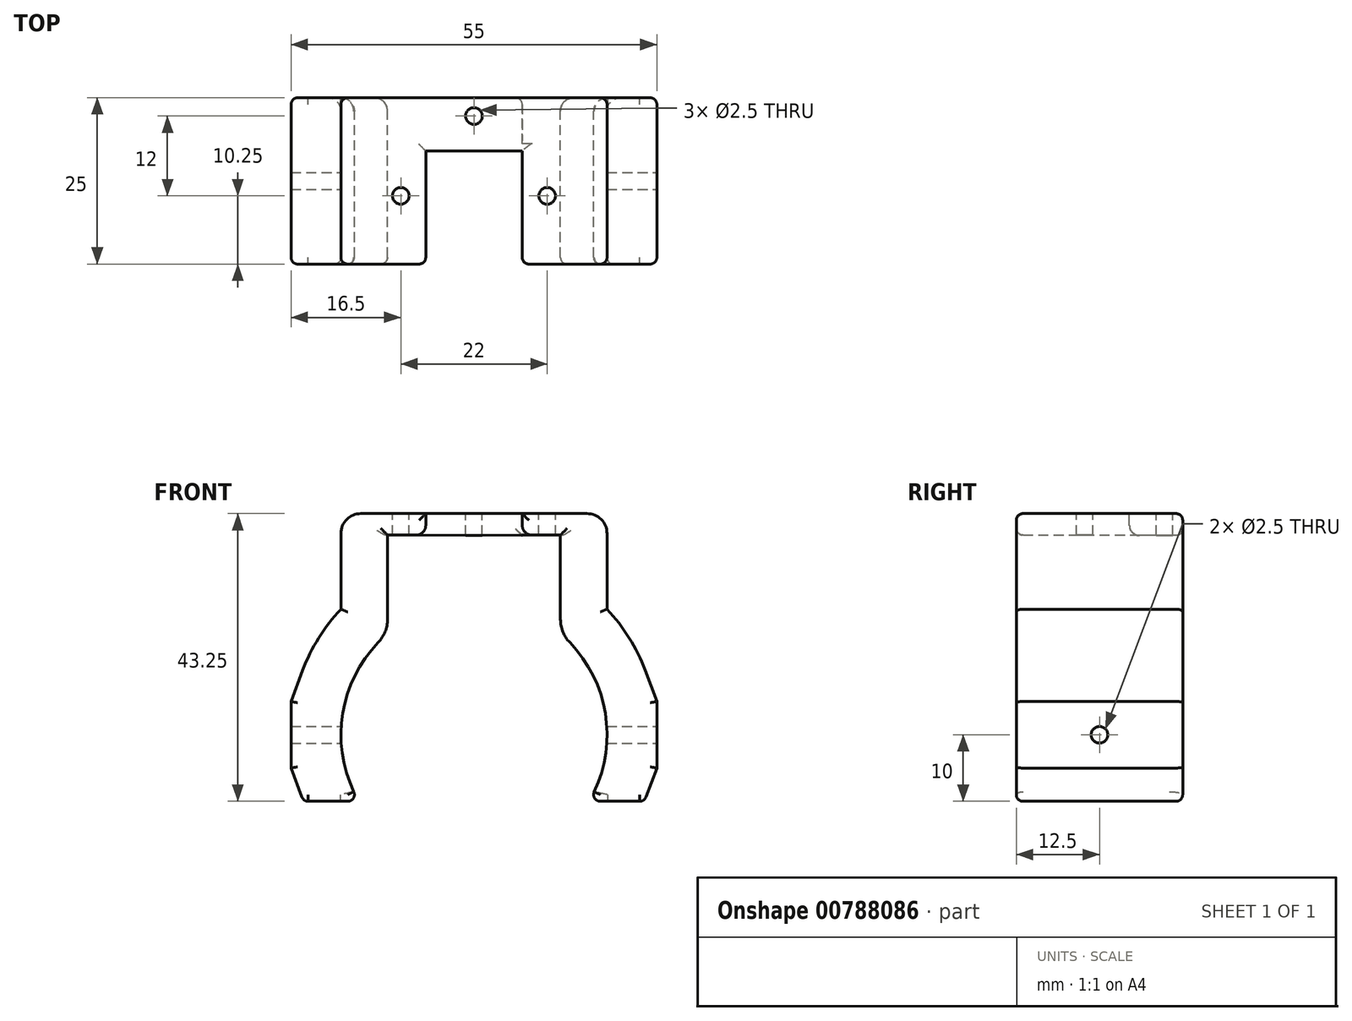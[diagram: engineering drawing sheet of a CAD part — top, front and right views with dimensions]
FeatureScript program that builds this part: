
annotation { "Feature Type Name" : "Feature", "Feature Type Description" : "" }
export const myFeature = defineFeature(function(context is Context, id is Id, definition is map)
    precondition{}
    {
        {
            var Q0;
            Q0=qCreatedBy(makeId("Front.planeOp"),FACE);
            var sketch = newSketch(context, id + "F0", { "sketchPlane" : qUnion([Q0])});
            skLineSegment(sketch, "E0", {"start": v(0, 0) * mm, "end": v(0, 1) * mm});
            skArc(sketch, "E1", {"start": v(-13, 16.2) * mm, "mid": v(0, -19) * mm, "end": v(13, 16.2) * mm});
            skArc(sketch, "E2.0", {"start": v(-20, 19.87) * mm, "mid": v(-23.33, 15.56) * mm, "end": v(-25.74, 10.68) * mm});
            skLineSegment(sketch, "E3", {"start": v(0, 0) * mm, "end": v(0, 15) * mm, "construction": true});
            skLineSegment(sketch, "E4", {"start": v(0, 15) * mm, "end": v(13, 15) * mm, "construction": true});
            skLineSegment(sketch, "E5.MirrorCS", {"start": v(0, 15) * mm, "end": v(-13, 15) * mm, "construction": true});
            skLineSegment(sketch, "E6", {"start": v(27.5, 1) * mm, "end": v(27.5, 6) * mm});
            skLineSegment(sketch, "E7", {"start": v(0, 1) * mm, "end": v(32.41, 1) * mm, "construction": true});
            skLineSegment(sketch, "E8", {"start": v(27.5, 6) * mm, "end": v(25.74, 10.68) * mm});
            skLineSegment(sketch, "E9.MirrorCS", {"start": v(27.5, -4) * mm, "end": v(25.74, -8.68) * mm});
            skLineSegment(sketch, "E10.MirrorCS", {"start": v(27.5, 1) * mm, "end": v(27.5, -4) * mm});
            skArc(sketch, "E11.trimOffspring", {"start": v(25.74, 10.68) * mm, "mid": v(23.33, 15.56) * mm, "end": v(20, 19.87) * mm});
            skLineSegment(sketch, "E12.MirrorCS", {"start": v(-27.5, 6) * mm, "end": v(-25.74, 10.68) * mm});
            skLineSegment(sketch, "E13.MirrorCS", {"start": v(-27.5, 1) * mm, "end": v(-27.5, 6) * mm});
            skLineSegment(sketch, "E14.MirrorCS", {"start": v(-27.5, 1) * mm, "end": v(-27.5, -4) * mm});
            skLineSegment(sketch, "E15.MirrorCS", {"start": v(-27.5, -4) * mm, "end": v(-25.74, -8.68) * mm});
            skArc(sketch, "E16.trimOffspring", {"start": v(-25.74, -8.68) * mm, "mid": v(-19.45, -18.45) * mm, "end": v(-9.68, -24.74) * mm});
            skLineSegment(sketch, "E17", {"start": v(0, 1) * mm, "end": v(-10.04, -9.04) * mm, "construction": true});
            skLineSegment(sketch, "E18.MirrorCS", {"start": v(5, -26.5) * mm, "end": v(9.68, -24.74) * mm});
            skLineSegment(sketch, "E19.MirrorCS", {"start": v(0, -26.5) * mm, "end": v(5, -26.5) * mm});
            skLineSegment(sketch, "E20.MirrorCS", {"start": v(0, -26.5) * mm, "end": v(-5, -26.5) * mm});
            skLineSegment(sketch, "E21.MirrorCS", {"start": v(-5, -26.5) * mm, "end": v(-9.68, -24.74) * mm});
            skArc(sketch, "E22.trimOffspring", {"start": v(9.68, -24.74) * mm, "mid": v(19.45, -18.45) * mm, "end": v(25.74, -8.68) * mm});
            skLineSegment(sketch, "E23", {"start": v(13, 16.2) * mm, "end": v(13, 25.23) * mm});
            skLineSegment(sketch, "E24", {"start": v(-13, 16.2) * mm, "end": v(-13, 25.23) * mm});
            skLineSegment(sketch, "E25", {"start": v(0, 1) * mm, "end": v(0, 31) * mm, "construction": true});
            skLineSegment(sketch, "E26", {"start": v(0, 31) * mm, "end": v(-7.25, 31) * mm, "construction": true});
            skLineSegment(sketch, "E27.MirrorCS", {"start": v(0, 31) * mm, "end": v(7.25, 31) * mm, "construction": true});
            skLineSegment(sketch, "E28", {"start": v(-13, 25.23) * mm, "end": v(-13, 31.02) * mm});
            skLineSegment(sketch, "E29", {"start": v(-13, 31.02) * mm, "end": v(-7.25, 31) * mm});
            skLineSegment(sketch, "E30", {"start": v(-20, 31.05) * mm, "end": v(-20, 19.87) * mm});
            skLineSegment(sketch, "E31", {"start": v(-7.25, 31) * mm, "end": v(-7.25, 34.25) * mm});
            skLineSegment(sketch, "E32", {"start": v(-7.25, 34.25) * mm, "end": v(-20, 34.25) * mm});
            skLineSegment(sketch, "E33", {"start": v(-20, 34.25) * mm, "end": v(-20, 31.05) * mm});
            skLineSegment(sketch, "E34.MirrorCS", {"start": v(13, 25.23) * mm, "end": v(13, 31.02) * mm});
            skLineSegment(sketch, "E35.MirrorCS", {"start": v(13, 31.02) * mm, "end": v(7.25, 31) * mm});
            skLineSegment(sketch, "E36.MirrorCS", {"start": v(7.25, 31) * mm, "end": v(7.25, 34.25) * mm});
            skLineSegment(sketch, "E37.MirrorCS", {"start": v(7.25, 34.25) * mm, "end": v(20, 34.25) * mm});
            skLineSegment(sketch, "E38.MirrorCS", {"start": v(20, 34.25) * mm, "end": v(20, 31.05) * mm});
            skLineSegment(sketch, "E39.MirrorCS", {"start": v(20, 31.05) * mm, "end": v(20, 19.87) * mm});
            skSolve(sketch);
        }
        {
            var Q0;
            Q0=makeQuery(id+"F0.imprint","IMPRINT",FACE,{"disambiguationData":[TD([[makeQuery(id+"F0.imprint","IMPRINT",EDGE,{"derivedFrom":sQuery(id+"F0.wireOp",EDGE,"E1")}),-1.0]])]});
            extrude(context, id + "F1", {"entities" : qUnion([Q0]), "depth" : 25 * mm, "offsetDistance" : 25 * mm});
        }
        {
            var Q0;
            Q0=makeQuery(id+"F1.opExtrude","SWEPT_FACE",FACE,{"disambiguationData":[OSD([sQuery(id+"F0.wireOp",EDGE,"E37.MirrorCS")])]});
            var sketch = newSketch(context, id + "F2", { "sketchPlane" : qUnion([Q0])});
            skLineSegment(sketch, "E40", {"start": v(0, 0) * mm, "end": v(0, -8) * mm, "construction": true});
            skLineSegment(sketch, "E41.0", {"start": v(-7.25, -25) * mm, "end": v(-7.25, 0) * mm});
            skLineSegment(sketch, "E42.0", {"start": v(7.25, -25) * mm, "end": v(7.25, 0) * mm});
            skLineSegment(sketch, "E43", {"start": v(7.25, 0) * mm, "end": v(-7.25, 0) * mm});
            skLineSegment(sketch, "E44", {"start": v(-7.25, -8) * mm, "end": v(7.25, -8) * mm});
            skSolve(sketch);
        }
        {
            var Q0;
            {var subQ0=sQuery(id+"F2.wireOp",EDGE,"E43");Q0=makeQuery(id+"F2.imprint","IMPRINT",FACE,{"disambiguationData":[TD([[makeQuery(id+"F2.imprint","IMPRINT",EDGE,{"derivedFrom":subQ0}),1.0]])]});}
            var Q1;
            Q1=makeQuery(id+"F1.opExtrude","SWEPT_FACE",FACE,{"disambiguationData":[OSD([sQuery(id+"F0.wireOp",EDGE,"E29")])]});
            extrude(context, id + "F3", {"entities" : qUnion([Q0]), "operationType" : NewBodyOperationType.ADD, "endBound" : BoundingType.UP_TO_SURFACE, "oppositeDirection" : true, "depth" : 25 * mm, "endBoundEntityFace" : qUnion([Q1]), "offsetDistance" : 25 * mm});
        }
        {
            var Q0;
            Q0=makeQuery(id+"F3.boolean.opBoolean","MERGE",FACE,{"derivedFrom":[makeQuery(id+"F1.opExtrude","SWEPT_FACE",FACE,{"disambiguationData":[OSD([sQuery(id+"F0.wireOp",EDGE,"E32")])]}),makeQuery(id+"F1.opExtrude","SWEPT_FACE",FACE,{"disambiguationData":[OSD([sQuery(id+"F0.wireOp",EDGE,"E37.MirrorCS")])]}),makeQuery(id+"F3.opExtrude","CAP_FACE",FACE,{"disambiguationData":[OSD([sQuery(id+"F2.wireOp",EDGE,"E41.0"),sQuery(id+"F2.wireOp",EDGE,"E42.0"),sQuery(id+"F2.wireOp",EDGE,"E43"),sQuery(id+"F2.wireOp",EDGE,"E44")])],"isStart":true})]});
            var sketch = newSketch(context, id + "F4", { "sketchPlane" : qUnion([Q0])});
            skLineSegment(sketch, "E45", {"start": v(0, 0) * mm, "end": v(0, -2.75) * mm, "construction": true});
            skLineSegment(sketch, "E46", {"start": v(0, -2.75) * mm, "end": v(-11, -2.75) * mm, "construction": true});
            skLineSegment(sketch, "E47", {"start": v(-11, -2.75) * mm, "end": v(-11, -14.75) * mm, "construction": true});
            skPoint(sketch, "E48", {"position": v(0, -2.75) * mm});
            skLineSegment(sketch, "E49.0.0", {"start": v(20, 0) * mm, "end": v(-20, 0) * mm});
            skLineSegment(sketch, "E49.0.1", {"start": v(-20, 0) * mm, "end": v(-20, -25) * mm});
            skLineSegment(sketch, "E49.0.2", {"start": v(-20, -25) * mm, "end": v(7.25, -25) * mm});
            skLineSegment(sketch, "E49.0.6", {"start": v(7.25, -25) * mm, "end": v(20, -25) * mm});
            skLineSegment(sketch, "E49.0.7", {"start": v(20, -25) * mm, "end": v(20, 0) * mm});
            skPoint(sketch, "E50.orphan", {"position": v(-7.25, -25) * mm});
            skLineSegment(sketch, "E51", {"start": v(0, -25) * mm, "end": v(0, 0) * mm, "construction": true});
            skPoint(sketch, "E52", {"position": v(0, -12.5) * mm});
            skPoint(sketch, "E53", {"position": v(-11, -14.75) * mm});
            skPoint(sketch, "E54.MirrorP", {"position": v(11, -14.75) * mm});
            skSolve(sketch);
        }
        {
            var Q0;
            Q0=sQuery(id+"F4.wireOp",VERTEX,"E53");
            var Q1;
            Q1=sQuery(id+"F4.wireOp",VERTEX,"E48");
            var Q2;
            Q2=sQuery(id+"F4.wireOp",VERTEX,"E54.MirrorP");
            var Q3;
            Q3=makeQuery(id+"F1.opExtrude","SWEPT_BODY",BODY,{"disambiguationData":[OSD([sQuery(id+"F0.wireOp",EDGE,"E1"),sQuery(id+"F0.wireOp",EDGE,"E2.0"),sQuery(id+"F0.wireOp",EDGE,"E6"),sQuery(id+"F0.wireOp",EDGE,"E8"),sQuery(id+"F0.wireOp",EDGE,"E9.MirrorCS"),sQuery(id+"F0.wireOp",EDGE,"E10.MirrorCS"),sQuery(id+"F0.wireOp",EDGE,"E11.trimOffspring"),sQuery(id+"F0.wireOp",EDGE,"E12.MirrorCS"),sQuery(id+"F0.wireOp",EDGE,"E13.MirrorCS"),sQuery(id+"F0.wireOp",EDGE,"E14.MirrorCS"),sQuery(id+"F0.wireOp",EDGE,"E15.MirrorCS"),sQuery(id+"F0.wireOp",EDGE,"E16.trimOffspring"),sQuery(id+"F0.wireOp",EDGE,"E18.MirrorCS"),sQuery(id+"F0.wireOp",EDGE,"E19.MirrorCS"),sQuery(id+"F0.wireOp",EDGE,"E20.MirrorCS"),sQuery(id+"F0.wireOp",EDGE,"E21.MirrorCS"),sQuery(id+"F0.wireOp",EDGE,"E22.trimOffspring"),sQuery(id+"F0.wireOp",EDGE,"E23"),sQuery(id+"F0.wireOp",EDGE,"E24"),sQuery(id+"F0.wireOp",EDGE,"E28"),sQuery(id+"F0.wireOp",EDGE,"E29"),sQuery(id+"F0.wireOp",EDGE,"E30"),sQuery(id+"F0.wireOp",EDGE,"E31"),sQuery(id+"F0.wireOp",EDGE,"E32"),sQuery(id+"F0.wireOp",EDGE,"E33"),sQuery(id+"F0.wireOp",EDGE,"E34.MirrorCS"),sQuery(id+"F0.wireOp",EDGE,"E35.MirrorCS"),sQuery(id+"F0.wireOp",EDGE,"E36.MirrorCS"),sQuery(id+"F0.wireOp",EDGE,"E37.MirrorCS"),sQuery(id+"F0.wireOp",EDGE,"E38.MirrorCS"),sQuery(id+"F0.wireOp",EDGE,"E39.MirrorCS")])]});
            hole(context, id + "F5", {"style" : HoleStyle.SIMPLE, "endStyle" : HoleEndStyle.BLIND, "standardTappedOrClearance" : lookupTablePath({ "standard" : "ISO", "engagement" : "75%", "pitch" : "0.5 mm", "size" : "M3", "type" : "Tapped" }), "standardBlindInLast" : lookupTablePath({ "standard" : "ISO", "engagement" : "75%", "pitch" : "0.5 mm", "size" : "M3", "type" : "Tapped" }), "holeDiameter" : 2.5 * mm, "majorDiameter" : 3 * mm, "showTappedDepth" : true, "holeDepth" : 4 * mm, "isTappedThrough" : true, "tappedDepth" : 2.5 * mm, "tapClearance" : 3, "locations" : qUnion([Q0, Q1, Q2]), "scope" : qUnion([Q3])});
        }
        {
            var Q0;
            Q0=sQuery(id+"F4.wireOp",VERTEX,"E52");
            var Q1;
            Q1=makeQuery(id+"F1.opExtrude","SWEPT_BODY",BODY,{"disambiguationData":[OSD([sQuery(id+"F0.wireOp",EDGE,"E1"),sQuery(id+"F0.wireOp",EDGE,"E2.0"),sQuery(id+"F0.wireOp",EDGE,"E6"),sQuery(id+"F0.wireOp",EDGE,"E8"),sQuery(id+"F0.wireOp",EDGE,"E9.MirrorCS"),sQuery(id+"F0.wireOp",EDGE,"E10.MirrorCS"),sQuery(id+"F0.wireOp",EDGE,"E11.trimOffspring"),sQuery(id+"F0.wireOp",EDGE,"E12.MirrorCS"),sQuery(id+"F0.wireOp",EDGE,"E13.MirrorCS"),sQuery(id+"F0.wireOp",EDGE,"E14.MirrorCS"),sQuery(id+"F0.wireOp",EDGE,"E15.MirrorCS"),sQuery(id+"F0.wireOp",EDGE,"E16.trimOffspring"),sQuery(id+"F0.wireOp",EDGE,"E18.MirrorCS"),sQuery(id+"F0.wireOp",EDGE,"E19.MirrorCS"),sQuery(id+"F0.wireOp",EDGE,"E20.MirrorCS"),sQuery(id+"F0.wireOp",EDGE,"E21.MirrorCS"),sQuery(id+"F0.wireOp",EDGE,"E22.trimOffspring"),sQuery(id+"F0.wireOp",EDGE,"E23"),sQuery(id+"F0.wireOp",EDGE,"E24"),sQuery(id+"F0.wireOp",EDGE,"E28"),sQuery(id+"F0.wireOp",EDGE,"E29"),sQuery(id+"F0.wireOp",EDGE,"E30"),sQuery(id+"F0.wireOp",EDGE,"E31"),sQuery(id+"F0.wireOp",EDGE,"E32"),sQuery(id+"F0.wireOp",EDGE,"E33"),sQuery(id+"F0.wireOp",EDGE,"E34.MirrorCS"),sQuery(id+"F0.wireOp",EDGE,"E35.MirrorCS"),sQuery(id+"F0.wireOp",EDGE,"E36.MirrorCS"),sQuery(id+"F0.wireOp",EDGE,"E37.MirrorCS"),sQuery(id+"F0.wireOp",EDGE,"E38.MirrorCS"),sQuery(id+"F0.wireOp",EDGE,"E39.MirrorCS")])]});
            hole(context, id + "F6", {"style" : HoleStyle.SIMPLE, "endStyle" : HoleEndStyle.THROUGH, "standardTappedOrClearance" : lookupTablePath({ "standard" : "ISO", "engagement" : "75%", "pitch" : "0.5 mm", "size" : "M3", "type" : "Tapped" }), "standardBlindInLast" : lookupTablePath({ "standard" : "ISO", "engagement" : "75%", "pitch" : "0.5 mm", "size" : "M3", "type" : "Tapped" }), "holeDiameter" : 2.5 * mm, "majorDiameter" : 3 * mm, "showTappedDepth" : true, "isTappedThrough" : true, "tappedDepth" : 2.5 * mm, "tapClearance" : 3, "locations" : qUnion([Q0]), "scope" : qUnion([Q1])});
        }
        {
            var Q0;
            Q0=makeQuery(id+"F1.opExtrude","SWEPT_FACE",FACE,{"disambiguationData":[OSD([sQuery(id+"F0.wireOp",EDGE,"E6"),sQuery(id+"F0.wireOp",EDGE,"E10.MirrorCS")])]});
            var sketch = newSketch(context, id + "F7", { "sketchPlane" : qUnion([Q0])});
            skLineSegment(sketch, "E55", {"start": v(-12.5, 6) * mm, "end": v(-12.5, -4) * mm, "construction": true});
            skPoint(sketch, "E56", {"position": v(-12.5, 1) * mm});
            skSolve(sketch);
        }
        {
            var Q0;
            Q0=sQuery(id+"F7.wireOp",VERTEX,"E56");
            var Q1;
            Q1=makeQuery(id+"F1.opExtrude","SWEPT_BODY",BODY,{"disambiguationData":[OSD([sQuery(id+"F0.wireOp",EDGE,"E1"),sQuery(id+"F0.wireOp",EDGE,"E2.0"),sQuery(id+"F0.wireOp",EDGE,"E6"),sQuery(id+"F0.wireOp",EDGE,"E8"),sQuery(id+"F0.wireOp",EDGE,"E9.MirrorCS"),sQuery(id+"F0.wireOp",EDGE,"E10.MirrorCS"),sQuery(id+"F0.wireOp",EDGE,"E11.trimOffspring"),sQuery(id+"F0.wireOp",EDGE,"E12.MirrorCS"),sQuery(id+"F0.wireOp",EDGE,"E13.MirrorCS"),sQuery(id+"F0.wireOp",EDGE,"E14.MirrorCS"),sQuery(id+"F0.wireOp",EDGE,"E15.MirrorCS"),sQuery(id+"F0.wireOp",EDGE,"E16.trimOffspring"),sQuery(id+"F0.wireOp",EDGE,"E18.MirrorCS"),sQuery(id+"F0.wireOp",EDGE,"E19.MirrorCS"),sQuery(id+"F0.wireOp",EDGE,"E20.MirrorCS"),sQuery(id+"F0.wireOp",EDGE,"E21.MirrorCS"),sQuery(id+"F0.wireOp",EDGE,"E22.trimOffspring"),sQuery(id+"F0.wireOp",EDGE,"E23"),sQuery(id+"F0.wireOp",EDGE,"E24"),sQuery(id+"F0.wireOp",EDGE,"E28"),sQuery(id+"F0.wireOp",EDGE,"E29"),sQuery(id+"F0.wireOp",EDGE,"E30"),sQuery(id+"F0.wireOp",EDGE,"E31"),sQuery(id+"F0.wireOp",EDGE,"E32"),sQuery(id+"F0.wireOp",EDGE,"E33"),sQuery(id+"F0.wireOp",EDGE,"E34.MirrorCS"),sQuery(id+"F0.wireOp",EDGE,"E35.MirrorCS"),sQuery(id+"F0.wireOp",EDGE,"E36.MirrorCS"),sQuery(id+"F0.wireOp",EDGE,"E37.MirrorCS"),sQuery(id+"F0.wireOp",EDGE,"E38.MirrorCS"),sQuery(id+"F0.wireOp",EDGE,"E39.MirrorCS")])]});
            hole(context, id + "F8", {"style" : HoleStyle.SIMPLE, "endStyle" : HoleEndStyle.THROUGH, "standardTappedOrClearance" : lookupTablePath({ "standard" : "ISO", "engagement" : "75%", "pitch" : "0.5 mm", "size" : "M3", "type" : "Tapped" }), "standardBlindInLast" : lookupTablePath({ "standard" : "ISO", "engagement" : "75%", "pitch" : "0.5 mm", "size" : "M3", "type" : "Tapped" }), "holeDiameter" : 2.5 * mm, "majorDiameter" : 3 * mm, "showTappedDepth" : true, "isTappedThrough" : true, "tappedDepth" : 2.5 * mm, "tapClearance" : 3, "locations" : qUnion([Q0]), "scope" : qUnion([Q1])});
        }
        {
            var Q0;
            Q0=makeQuery(id+"F1.opExtrude","SWEPT_EDGE",EDGE,{"disambiguationData":[OSD([sQuery(id+"F0.wireOp",EDGE,"E1"),sQuery(id+"F0.wireOp",EDGE,"E23")])]});
            var Q1;
            Q1=makeQuery(id+"F1.opExtrude","SWEPT_EDGE",EDGE,{"disambiguationData":[OSD([sQuery(id+"F0.wireOp",EDGE,"E1"),sQuery(id+"F0.wireOp",EDGE,"E24")])]});
            fillet(context, id + "F9", {"entities" : qUnion([Q0, Q1]), "radius" : 5 * mm, "tangentPropagation" : true, "allowEdgeOverflow" : false});
        }
        {
            var Q0;
            Q0=makeQuery(id+"F1.opExtrude","CAP_EDGE",EDGE,{"disambiguationData":[OSD([sQuery(id+"F0.wireOp",EDGE,"E1")])],"isStart":true});
            fillet(context, id + "F10", {"entities" : qUnion([Q0]), "radius" : 2 * mm, "tangentPropagation" : true, "allowEdgeOverflow" : false});
        }
        {
            var Q0;
            Q0=makeQuery(id+"F1.opExtrude","SWEPT_EDGE",EDGE,{"disambiguationData":[OSD([sQuery(id+"F0.wireOp",EDGE,"E29"),sQuery(id+"F0.wireOp",EDGE,"E31")])]});
            var Q1;
            Q1=makeQuery(id+"F3.opExtrude","CAP_EDGE",EDGE,{"disambiguationData":[OSD([sQuery(id+"F2.wireOp",EDGE,"E44")])],"isStart":false});
            var Q2;
            {var subQ0=sQuery(id+"F0.wireOp",EDGE,"E35.MirrorCS");var subQ1=sQuery(id+"F0.wireOp",EDGE,"E36.MirrorCS");Q2=makeQuery(id+"F3.boolean.opBoolean","SPLIT",EDGE,{"disambiguationData":[topologyDisambiguationEdgeConnected([makeQuery(id+"F1.opExtrude","SWEPT_FACE",FACE,{"disambiguationData":[OSD([subQ1])]})])],"derivedFrom":makeQuery(id+"F1.opExtrude","SWEPT_EDGE",EDGE,{"disambiguationData":[OSD([subQ0,subQ1])]})});}
            fillet(context, id + "F11", {"entities" : qUnion([Q0, Q1, Q2]), "radius" : 1.5 * mm, "tangentPropagation" : true, "allowEdgeOverflow" : false});
        }
        {
            var Q0;
            Q0=makeQuery(id+"F3.boolean.opBoolean","MERGE",FACE,{"derivedFrom":[makeQuery(id+"F1.opExtrude","CAP_FACE",FACE,{"disambiguationData":[OSD([sQuery(id+"F0.wireOp",EDGE,"E1"),sQuery(id+"F0.wireOp",EDGE,"E2.0"),sQuery(id+"F0.wireOp",EDGE,"E6"),sQuery(id+"F0.wireOp",EDGE,"E8"),sQuery(id+"F0.wireOp",EDGE,"E9.MirrorCS"),sQuery(id+"F0.wireOp",EDGE,"E10.MirrorCS"),sQuery(id+"F0.wireOp",EDGE,"E11.trimOffspring"),sQuery(id+"F0.wireOp",EDGE,"E12.MirrorCS"),sQuery(id+"F0.wireOp",EDGE,"E13.MirrorCS"),sQuery(id+"F0.wireOp",EDGE,"E14.MirrorCS"),sQuery(id+"F0.wireOp",EDGE,"E15.MirrorCS"),sQuery(id+"F0.wireOp",EDGE,"E16.trimOffspring"),sQuery(id+"F0.wireOp",EDGE,"E18.MirrorCS"),sQuery(id+"F0.wireOp",EDGE,"E19.MirrorCS"),sQuery(id+"F0.wireOp",EDGE,"E20.MirrorCS"),sQuery(id+"F0.wireOp",EDGE,"E21.MirrorCS"),sQuery(id+"F0.wireOp",EDGE,"E22.trimOffspring"),sQuery(id+"F0.wireOp",EDGE,"E23"),sQuery(id+"F0.wireOp",EDGE,"E24"),sQuery(id+"F0.wireOp",EDGE,"E28"),sQuery(id+"F0.wireOp",EDGE,"E29"),sQuery(id+"F0.wireOp",EDGE,"E30"),sQuery(id+"F0.wireOp",EDGE,"E31"),sQuery(id+"F0.wireOp",EDGE,"E32"),sQuery(id+"F0.wireOp",EDGE,"E33"),sQuery(id+"F0.wireOp",EDGE,"E34.MirrorCS"),sQuery(id+"F0.wireOp",EDGE,"E35.MirrorCS"),sQuery(id+"F0.wireOp",EDGE,"E36.MirrorCS"),sQuery(id+"F0.wireOp",EDGE,"E37.MirrorCS"),sQuery(id+"F0.wireOp",EDGE,"E38.MirrorCS"),sQuery(id+"F0.wireOp",EDGE,"E39.MirrorCS")])],"isStart":true}),makeQuery(id+"F3.opExtrude","SWEPT_FACE",FACE,{"disambiguationData":[OSD([sQuery(id+"F2.wireOp",EDGE,"E43")])]})]});
            var sketch = newSketch(context, id + "F12", { "sketchPlane" : qUnion([Q0])});
            skLineSegment(sketch, "E57", {"start": v(0, 0) * mm, "end": v(0, -9) * mm});
            skPoint(sketch, "E57.endSnap0", {"position": v(0, -25.5) * mm});
            skLineSegment(sketch, "E58", {"start": v(0, -9) * mm, "end": v(36.24, -9) * mm});
            skLineSegment(sketch, "E59", {"start": v(36.24, -9) * mm, "end": v(36.24, -30) * mm});
            skLineSegment(sketch, "E60", {"start": v(36.24, -30) * mm, "end": v(-35.5, -30) * mm});
            skLineSegment(sketch, "E61", {"start": v(-35.5, -30) * mm, "end": v(-35.5, -9) * mm});
            skLineSegment(sketch, "E62", {"start": v(-35.5, -9) * mm, "end": v(0, -9) * mm});
            skSolve(sketch);
        }
        {
            var Q0;
            Q0 = qSketchRegion(id + "F12", true);
            extrude(context, id + "F13", {"entities" : qUnion([Q0]), "operationType" : NewBodyOperationType.REMOVE, "oppositeDirection" : true, "depth" : 43 * mm, "offsetDistance" : 25 * mm});
        }
        {
            var Q0;
            Q0=makeQuery(id+"F13.boolean.opBoolean","INTERSECT",EDGE,{"disambiguationData":[OD(0.0)],"derivedFrom":[makeQuery(id+"F1.opExtrude","SWEPT_FACE",FACE,{"disambiguationData":[OSD([sQuery(id+"F0.wireOp",EDGE,"E1")])]}),makeQuery(id+"F13.opExtrude","SWEPT_FACE",FACE,{"disambiguationData":[OSD([sQuery(id+"F12.wireOp",EDGE,"E58"),sQuery(id+"F12.wireOp",EDGE,"E62")])]})]});
            var Q1;
            Q1=makeQuery(id+"F13.boolean.opBoolean","INTERSECT",EDGE,{"disambiguationData":[OD(1.0)],"derivedFrom":[makeQuery(id+"F1.opExtrude","SWEPT_FACE",FACE,{"disambiguationData":[OSD([sQuery(id+"F0.wireOp",EDGE,"E1")])]}),makeQuery(id+"F13.opExtrude","SWEPT_FACE",FACE,{"disambiguationData":[OSD([sQuery(id+"F12.wireOp",EDGE,"E58"),sQuery(id+"F12.wireOp",EDGE,"E62")])]})]});
            var Q2;
            {var subQ0=sQuery(id+"F0.wireOp",EDGE,"E16.trimOffspring");var subQ2=sQuery(id+"F12.wireOp",EDGE,"E62");var subQ3=sQuery(id+"F12.wireOp",EDGE,"E58");Q2=makeQuery(id+"F13.boolean.opBoolean","COPY",EDGE,{"disambiguationData":[TD([makeQuery(id+"FjdppgESHP8ERgp_1.opFillet","BLEND_FACE",FACE,{"disambiguationData":[OSD([subQ0]),TDD([makeQuery(id+"F1.opExtrude","CAP_EDGE",EDGE,{"disambiguationData":[OSD([subQ0])],"isStart":true})])]})])],"derivedFrom":makeQuery(id+"F13.opExtrude","CAP_EDGE",EDGE,{"disambiguationData":[OSD([subQ3,subQ2])],"isStart":true})});}
            var Q3;
            Q3=makeQuery(id+"F13.boolean.opBoolean","INTERSECT",EDGE,{"disambiguationData":[OD(0.0)],"derivedFrom":[makeQuery(id+"F10.opFillet","BLEND_FACE",FACE,{"disambiguationData":[OSD([sQuery(id+"F0.wireOp",EDGE,"E1")])]}),makeQuery(id+"F13.opExtrude","SWEPT_FACE",FACE,{"disambiguationData":[OSD([sQuery(id+"F12.wireOp",EDGE,"E58"),sQuery(id+"F12.wireOp",EDGE,"E62")])]})]});
            var Q4;
            {var subQ1=sQuery(id+"F0.wireOp",EDGE,"E22.trimOffspring");var subQ2=sQuery(id+"F12.wireOp",EDGE,"E62");var subQ3=sQuery(id+"F12.wireOp",EDGE,"E58");Q4=makeQuery(id+"F13.boolean.opBoolean","COPY",EDGE,{"disambiguationData":[TD([makeQuery(id+"FjdppgESHP8ERgp_1.opFillet","BLEND_FACE",FACE,{"disambiguationData":[OSD([subQ1]),TDD([makeQuery(id+"F1.opExtrude","CAP_EDGE",EDGE,{"disambiguationData":[OSD([subQ1])],"isStart":true})])]})])],"derivedFrom":makeQuery(id+"F13.opExtrude","CAP_EDGE",EDGE,{"disambiguationData":[OSD([subQ3,subQ2])],"isStart":true})});}
            var Q5;
            Q5=makeQuery(id+"F13.boolean.opBoolean","INTERSECT",EDGE,{"disambiguationData":[OD(1.0)],"derivedFrom":[makeQuery(id+"FxoKyTsDUUiXwgX_1.opFillet","BLEND_FACE",FACE,{"disambiguationData":[OSD([sQuery(id+"F0.wireOp",EDGE,"E1")])]}),makeQuery(id+"F13.opExtrude","SWEPT_FACE",FACE,{"disambiguationData":[OSD([sQuery(id+"F12.wireOp",EDGE,"E58"),sQuery(id+"F12.wireOp",EDGE,"E62")])]})]});
            var Q6;
            Q6=makeQuery(id+"F13.boolean.opBoolean","INTERSECT",EDGE,{"disambiguationData":[OD(1.0)],"derivedFrom":[makeQuery(id+"F1.opExtrude","CAP_FACE",FACE,{"disambiguationData":[OSD([sQuery(id+"F0.wireOp",EDGE,"E1"),sQuery(id+"F0.wireOp",EDGE,"E2.0"),sQuery(id+"F0.wireOp",EDGE,"E6"),sQuery(id+"F0.wireOp",EDGE,"E8"),sQuery(id+"F0.wireOp",EDGE,"E9.MirrorCS"),sQuery(id+"F0.wireOp",EDGE,"E10.MirrorCS"),sQuery(id+"F0.wireOp",EDGE,"E11.trimOffspring"),sQuery(id+"F0.wireOp",EDGE,"E12.MirrorCS"),sQuery(id+"F0.wireOp",EDGE,"E13.MirrorCS"),sQuery(id+"F0.wireOp",EDGE,"E14.MirrorCS"),sQuery(id+"F0.wireOp",EDGE,"E15.MirrorCS"),sQuery(id+"F0.wireOp",EDGE,"E16.trimOffspring"),sQuery(id+"F0.wireOp",EDGE,"E18.MirrorCS"),sQuery(id+"F0.wireOp",EDGE,"E19.MirrorCS"),sQuery(id+"F0.wireOp",EDGE,"E20.MirrorCS"),sQuery(id+"F0.wireOp",EDGE,"E21.MirrorCS"),sQuery(id+"F0.wireOp",EDGE,"E22.trimOffspring"),sQuery(id+"F0.wireOp",EDGE,"E23"),sQuery(id+"F0.wireOp",EDGE,"E24"),sQuery(id+"F0.wireOp",EDGE,"E28"),sQuery(id+"F0.wireOp",EDGE,"E29"),sQuery(id+"F0.wireOp",EDGE,"E30"),sQuery(id+"F0.wireOp",EDGE,"E31"),sQuery(id+"F0.wireOp",EDGE,"E32"),sQuery(id+"F0.wireOp",EDGE,"E33"),sQuery(id+"F0.wireOp",EDGE,"E34.MirrorCS"),sQuery(id+"F0.wireOp",EDGE,"E35.MirrorCS"),sQuery(id+"F0.wireOp",EDGE,"E36.MirrorCS"),sQuery(id+"F0.wireOp",EDGE,"E37.MirrorCS"),sQuery(id+"F0.wireOp",EDGE,"E38.MirrorCS"),sQuery(id+"F0.wireOp",EDGE,"E39.MirrorCS")])],"isStart":false}),makeQuery(id+"F13.opExtrude","SWEPT_FACE",FACE,{"disambiguationData":[OSD([sQuery(id+"F12.wireOp",EDGE,"E58"),sQuery(id+"F12.wireOp",EDGE,"E62")])]})]});
            var Q7;
            Q7=makeQuery(id+"F13.boolean.opBoolean","INTERSECT",EDGE,{"disambiguationData":[OD(1.0)],"derivedFrom":[makeQuery(id+"F10.opFillet","BLEND_FACE",FACE,{"disambiguationData":[OSD([sQuery(id+"F0.wireOp",EDGE,"E1")])]}),makeQuery(id+"F13.opExtrude","SWEPT_FACE",FACE,{"disambiguationData":[OSD([sQuery(id+"F12.wireOp",EDGE,"E58"),sQuery(id+"F12.wireOp",EDGE,"E62")])]})]});
            var Q8;
            Q8=makeQuery(id+"F13.boolean.opBoolean","INTERSECT",EDGE,{"disambiguationData":[OD(0.0)],"derivedFrom":[makeQuery(id+"FxoKyTsDUUiXwgX_1.opFillet","BLEND_FACE",FACE,{"disambiguationData":[OSD([sQuery(id+"F0.wireOp",EDGE,"E1")])]}),makeQuery(id+"F13.opExtrude","SWEPT_FACE",FACE,{"disambiguationData":[OSD([sQuery(id+"F12.wireOp",EDGE,"E58"),sQuery(id+"F12.wireOp",EDGE,"E62")])]})]});
            var Q9;
            Q9=makeQuery(id+"F13.boolean.opBoolean","INTERSECT",EDGE,{"disambiguationData":[OD(0.0)],"derivedFrom":[makeQuery(id+"F1.opExtrude","CAP_FACE",FACE,{"disambiguationData":[OSD([sQuery(id+"F0.wireOp",EDGE,"E1"),sQuery(id+"F0.wireOp",EDGE,"E2.0"),sQuery(id+"F0.wireOp",EDGE,"E6"),sQuery(id+"F0.wireOp",EDGE,"E8"),sQuery(id+"F0.wireOp",EDGE,"E9.MirrorCS"),sQuery(id+"F0.wireOp",EDGE,"E10.MirrorCS"),sQuery(id+"F0.wireOp",EDGE,"E11.trimOffspring"),sQuery(id+"F0.wireOp",EDGE,"E12.MirrorCS"),sQuery(id+"F0.wireOp",EDGE,"E13.MirrorCS"),sQuery(id+"F0.wireOp",EDGE,"E14.MirrorCS"),sQuery(id+"F0.wireOp",EDGE,"E15.MirrorCS"),sQuery(id+"F0.wireOp",EDGE,"E16.trimOffspring"),sQuery(id+"F0.wireOp",EDGE,"E18.MirrorCS"),sQuery(id+"F0.wireOp",EDGE,"E19.MirrorCS"),sQuery(id+"F0.wireOp",EDGE,"E20.MirrorCS"),sQuery(id+"F0.wireOp",EDGE,"E21.MirrorCS"),sQuery(id+"F0.wireOp",EDGE,"E22.trimOffspring"),sQuery(id+"F0.wireOp",EDGE,"E23"),sQuery(id+"F0.wireOp",EDGE,"E24"),sQuery(id+"F0.wireOp",EDGE,"E28"),sQuery(id+"F0.wireOp",EDGE,"E29"),sQuery(id+"F0.wireOp",EDGE,"E30"),sQuery(id+"F0.wireOp",EDGE,"E31"),sQuery(id+"F0.wireOp",EDGE,"E32"),sQuery(id+"F0.wireOp",EDGE,"E33"),sQuery(id+"F0.wireOp",EDGE,"E34.MirrorCS"),sQuery(id+"F0.wireOp",EDGE,"E35.MirrorCS"),sQuery(id+"F0.wireOp",EDGE,"E36.MirrorCS"),sQuery(id+"F0.wireOp",EDGE,"E37.MirrorCS"),sQuery(id+"F0.wireOp",EDGE,"E38.MirrorCS"),sQuery(id+"F0.wireOp",EDGE,"E39.MirrorCS")])],"isStart":false}),makeQuery(id+"F13.opExtrude","SWEPT_FACE",FACE,{"disambiguationData":[OSD([sQuery(id+"F12.wireOp",EDGE,"E58"),sQuery(id+"F12.wireOp",EDGE,"E62")])]})]});
            fillet(context, id + "F14", {"entities" : qUnion([Q0, Q1, Q2, Q3, Q4, Q5, Q6, Q7, Q8, Q9]), "radius" : 1 * mm, "tangentPropagation" : true, "allowEdgeOverflow" : false});
        }
        {
            var Q0;
            Q0=makeQuery(id+"F1.opExtrude","SWEPT_EDGE",EDGE,{"disambiguationData":[OSD([sQuery(id+"F0.wireOp",EDGE,"E32"),sQuery(id+"F0.wireOp",EDGE,"E33")])]});
            var Q1;
            Q1=makeQuery(id+"F1.opExtrude","SWEPT_EDGE",EDGE,{"disambiguationData":[OSD([sQuery(id+"F0.wireOp",EDGE,"E37.MirrorCS"),sQuery(id+"F0.wireOp",EDGE,"E38.MirrorCS")])]});
            fillet(context, id + "F15", {"entities" : qUnion([Q0, Q1]), "radius" : 3 * mm, "tangentPropagation" : true, "allowEdgeOverflow" : false});
        }
        {
            var Q0;
            {var subQ0=sQuery(id+"F0.wireOp",EDGE,"E29");var subQ1=sQuery(id+"F0.wireOp",EDGE,"E28");var subQ2=sQuery(id+"F0.wireOp",EDGE,"E24");var subQ3=sQuery(id+"F0.wireOp",EDGE,"E15.MirrorCS");var subQ4=sQuery(id+"F0.wireOp",EDGE,"E16.trimOffspring");var subQ5=sQuery(id+"F0.wireOp",EDGE,"E1");var subQ6=sQuery(id+"F0.wireOp",EDGE,"E2.0");var subQ7=sQuery(id+"F0.wireOp",EDGE,"E31");var subQ8=sQuery(id+"F0.wireOp",EDGE,"E33");var subQ9=sQuery(id+"F0.wireOp",EDGE,"E30");var subQ10=sQuery(id+"F0.wireOp",EDGE,"E12.MirrorCS");var subQ11=sQuery(id+"F0.wireOp",EDGE,"E14.MirrorCS");var subQ12=sQuery(id+"F0.wireOp",EDGE,"E13.MirrorCS");var subQ13=sQuery(id+"F0.wireOp",EDGE,"E32");var subQ14=sQuery(id+"F0.wireOp",EDGE,"E37.MirrorCS");Q0=makeQuery(id+"F13.boolean.opBoolean","SPLIT",FACE,{"disambiguationData":[TD([makeQuery(id+"F1.opExtrude","SWEPT_FACE",FACE,{"disambiguationData":[OSD([subQ6])]})])],"derivedFrom":makeQuery(id+"F1.opExtrude","CAP_FACE",FACE,{"disambiguationData":[OSD([subQ5,subQ6,sQuery(id+"F0.wireOp",EDGE,"E6"),sQuery(id+"F0.wireOp",EDGE,"E8"),sQuery(id+"F0.wireOp",EDGE,"E9.MirrorCS"),sQuery(id+"F0.wireOp",EDGE,"E10.MirrorCS"),sQuery(id+"F0.wireOp",EDGE,"E11.trimOffspring"),subQ10,subQ12,subQ11,subQ3,subQ4,sQuery(id+"F0.wireOp",EDGE,"E18.MirrorCS"),sQuery(id+"F0.wireOp",EDGE,"E19.MirrorCS"),sQuery(id+"F0.wireOp",EDGE,"E20.MirrorCS"),sQuery(id+"F0.wireOp",EDGE,"E21.MirrorCS"),sQuery(id+"F0.wireOp",EDGE,"E22.trimOffspring"),sQuery(id+"F0.wireOp",EDGE,"E23"),subQ2,subQ1,subQ0,subQ9,subQ7,subQ13,subQ8,sQuery(id+"F0.wireOp",EDGE,"E34.MirrorCS"),sQuery(id+"F0.wireOp",EDGE,"E35.MirrorCS"),sQuery(id+"F0.wireOp",EDGE,"E36.MirrorCS"),subQ14,sQuery(id+"F0.wireOp",EDGE,"E38.MirrorCS"),sQuery(id+"F0.wireOp",EDGE,"E39.MirrorCS")])],"isStart":false})});}
            var Q1;
            Q1=makeQuery(id+"F3.boolean.opBoolean","MERGE",FACE,{"derivedFrom":[makeQuery(id+"F1.opExtrude","CAP_FACE",FACE,{"disambiguationData":[OSD([sQuery(id+"F0.wireOp",EDGE,"E1"),sQuery(id+"F0.wireOp",EDGE,"E2.0"),sQuery(id+"F0.wireOp",EDGE,"E6"),sQuery(id+"F0.wireOp",EDGE,"E8"),sQuery(id+"F0.wireOp",EDGE,"E9.MirrorCS"),sQuery(id+"F0.wireOp",EDGE,"E10.MirrorCS"),sQuery(id+"F0.wireOp",EDGE,"E11.trimOffspring"),sQuery(id+"F0.wireOp",EDGE,"E12.MirrorCS"),sQuery(id+"F0.wireOp",EDGE,"E13.MirrorCS"),sQuery(id+"F0.wireOp",EDGE,"E14.MirrorCS"),sQuery(id+"F0.wireOp",EDGE,"E15.MirrorCS"),sQuery(id+"F0.wireOp",EDGE,"E16.trimOffspring"),sQuery(id+"F0.wireOp",EDGE,"E18.MirrorCS"),sQuery(id+"F0.wireOp",EDGE,"E19.MirrorCS"),sQuery(id+"F0.wireOp",EDGE,"E20.MirrorCS"),sQuery(id+"F0.wireOp",EDGE,"E21.MirrorCS"),sQuery(id+"F0.wireOp",EDGE,"E22.trimOffspring"),sQuery(id+"F0.wireOp",EDGE,"E23"),sQuery(id+"F0.wireOp",EDGE,"E24"),sQuery(id+"F0.wireOp",EDGE,"E28"),sQuery(id+"F0.wireOp",EDGE,"E29"),sQuery(id+"F0.wireOp",EDGE,"E30"),sQuery(id+"F0.wireOp",EDGE,"E31"),sQuery(id+"F0.wireOp",EDGE,"E32"),sQuery(id+"F0.wireOp",EDGE,"E33"),sQuery(id+"F0.wireOp",EDGE,"E34.MirrorCS"),sQuery(id+"F0.wireOp",EDGE,"E35.MirrorCS"),sQuery(id+"F0.wireOp",EDGE,"E36.MirrorCS"),sQuery(id+"F0.wireOp",EDGE,"E37.MirrorCS"),sQuery(id+"F0.wireOp",EDGE,"E38.MirrorCS"),sQuery(id+"F0.wireOp",EDGE,"E39.MirrorCS")])],"isStart":true}),makeQuery(id+"F3.opExtrude","SWEPT_FACE",FACE,{"disambiguationData":[OSD([sQuery(id+"F2.wireOp",EDGE,"E43")])]})]});
            var Q2;
            {var subQ0=sQuery(id+"F0.wireOp",EDGE,"E36.MirrorCS");var subQ1=sQuery(id+"F0.wireOp",EDGE,"E1");var subQ2=sQuery(id+"F0.wireOp",EDGE,"E32");var subQ3=sQuery(id+"F0.wireOp",EDGE,"E11.trimOffspring");var subQ4=sQuery(id+"F0.wireOp",EDGE,"E35.MirrorCS");var subQ5=sQuery(id+"F0.wireOp",EDGE,"E34.MirrorCS");var subQ6=sQuery(id+"F0.wireOp",EDGE,"E23");var subQ7=sQuery(id+"F0.wireOp",EDGE,"E8");var subQ8=sQuery(id+"F0.wireOp",EDGE,"E22.trimOffspring");var subQ9=sQuery(id+"F0.wireOp",EDGE,"E10.MirrorCS");var subQ10=sQuery(id+"F0.wireOp",EDGE,"E6");var subQ11=sQuery(id+"F0.wireOp",EDGE,"E9.MirrorCS");var subQ12=sQuery(id+"F0.wireOp",EDGE,"E37.MirrorCS");var subQ13=sQuery(id+"F0.wireOp",EDGE,"E39.MirrorCS");var subQ14=sQuery(id+"F0.wireOp",EDGE,"E38.MirrorCS");Q2=makeQuery(id+"F13.boolean.opBoolean","SPLIT",FACE,{"disambiguationData":[TD([makeQuery(id+"F1.opExtrude","SWEPT_FACE",FACE,{"disambiguationData":[OSD([subQ7])]})])],"derivedFrom":makeQuery(id+"F1.opExtrude","CAP_FACE",FACE,{"disambiguationData":[OSD([subQ1,sQuery(id+"F0.wireOp",EDGE,"E2.0"),subQ10,subQ7,subQ11,subQ9,subQ3,sQuery(id+"F0.wireOp",EDGE,"E12.MirrorCS"),sQuery(id+"F0.wireOp",EDGE,"E13.MirrorCS"),sQuery(id+"F0.wireOp",EDGE,"E14.MirrorCS"),sQuery(id+"F0.wireOp",EDGE,"E15.MirrorCS"),sQuery(id+"F0.wireOp",EDGE,"E16.trimOffspring"),sQuery(id+"F0.wireOp",EDGE,"E18.MirrorCS"),sQuery(id+"F0.wireOp",EDGE,"E19.MirrorCS"),sQuery(id+"F0.wireOp",EDGE,"E20.MirrorCS"),sQuery(id+"F0.wireOp",EDGE,"E21.MirrorCS"),subQ8,subQ6,sQuery(id+"F0.wireOp",EDGE,"E24"),sQuery(id+"F0.wireOp",EDGE,"E28"),sQuery(id+"F0.wireOp",EDGE,"E29"),sQuery(id+"F0.wireOp",EDGE,"E30"),sQuery(id+"F0.wireOp",EDGE,"E31"),subQ2,sQuery(id+"F0.wireOp",EDGE,"E33"),subQ5,subQ4,subQ0,subQ12,subQ14,subQ13])],"isStart":false})});}
            fillet(context, id + "F16", {"entities" : qUnion([Q0, Q1, Q2]), "radius" : 1 * mm, "tangentPropagation" : true, "allowEdgeOverflow" : false});
        }
    });
